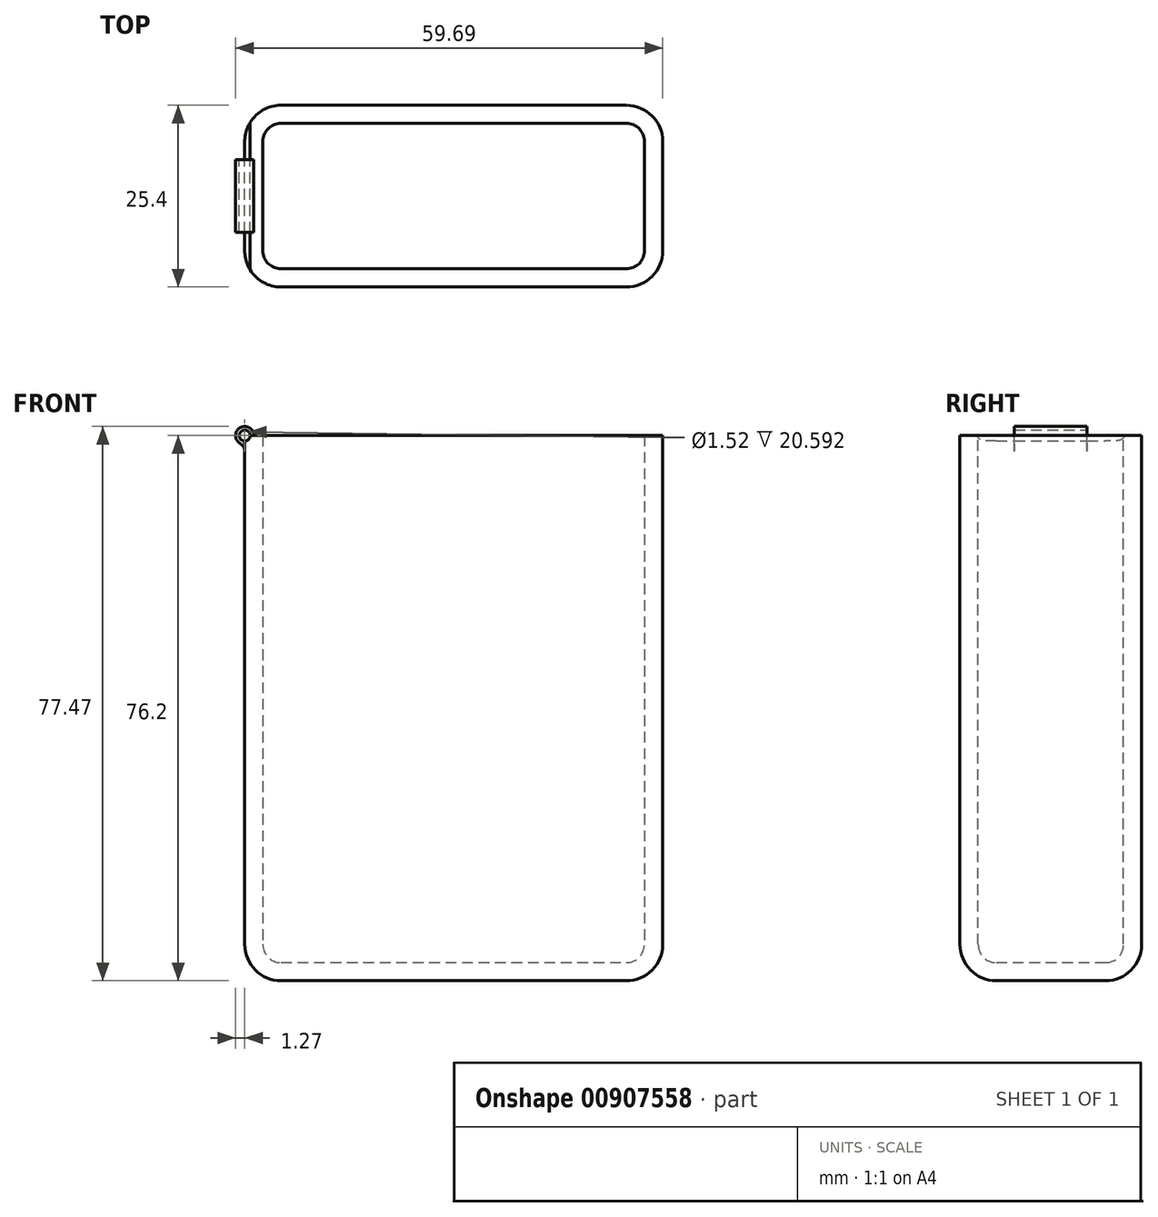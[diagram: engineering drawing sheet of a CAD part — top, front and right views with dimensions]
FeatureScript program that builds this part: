
annotation { "Feature Type Name" : "Feature", "Feature Type Description" : "" }
export const myFeature = defineFeature(function(context is Context, id is Id, definition is map)
    precondition{}
    {
        {
            var Q0;
            Q0=qCreatedBy(makeId("Front.planeOp"),FACE);
            var sketch = newSketch(context, id + "F0", { "sketchPlane" : qUnion([Q0])});
            skLineSegment(sketch, "E0.bottom", {"start": v(-29.21, 38.1) * mm, "end": v(29.21, 38.1) * mm});
            skLineSegment(sketch, "E0.top", {"start": v(-29.2, -38.1) * mm, "end": v(29.21, -38.1) * mm});
            skLineSegment(sketch, "E0.left", {"start": v(-29.21, 38.1) * mm, "end": v(-29.2, -38.1) * mm});
            skLineSegment(sketch, "E0.right", {"start": v(29.2, 38.1) * mm, "end": v(29.21, -38.1) * mm});
            skSolve(sketch);
        }
        {
            var Q0;
            Q0 = qSketchRegion(id + "F0", true);
            extrude(context, id + "F1", {"entities" : qUnion([Q0]), "depth" : 25.4 * mm, "offsetDistance" : 25.4 * mm});
        }
        {
            var Q0;
            Q0=makeQuery(id+"F1.opExtrude","CAP_EDGE",EDGE,{"disambiguationData":[OSD([sQuery(id+"F0.wireOp",EDGE,"E0.left")])],"isStart":false});
            var Q1;
            Q1=makeQuery(id+"F1.opExtrude","CAP_EDGE",EDGE,{"disambiguationData":[OSD([sQuery(id+"F0.wireOp",EDGE,"E0.right")])],"isStart":false});
            var Q2;
            Q2=makeQuery(id+"F1.opExtrude","CAP_EDGE",EDGE,{"disambiguationData":[OSD([sQuery(id+"F0.wireOp",EDGE,"E0.right")])],"isStart":true});
            var Q3;
            Q3=makeQuery(id+"F1.opExtrude","CAP_EDGE",EDGE,{"disambiguationData":[OSD([sQuery(id+"F0.wireOp",EDGE,"E0.left")])],"isStart":true});
            var Q4;
            Q4=makeQuery(id+"F1.opExtrude","SWEPT_FACE",FACE,{"disambiguationData":[OSD([sQuery(id+"F0.wireOp",EDGE,"E0.top")])]});
            fillet(context, id + "F2", {"entities" : qUnion([Q0, Q1, Q2, Q3, Q4]), "radius" : 5.08 * mm, "tangentPropagation" : true, "allowEdgeOverflow" : false});
        }
        {
            var Q0;
            Q0=makeQuery(id+"F1.opExtrude","SWEPT_FACE",FACE,{"disambiguationData":[OSD([sQuery(id+"F0.wireOp",EDGE,"E0.bottom")])]});
            shell(context, id + "F3", {"entities" : qUnion([Q0]), "thickness" : 2.54 * mm});
        }
        {
            var Q0;
            Q0=makeQuery(id+"F1.opExtrude","CAP_FACE",FACE,{"disambiguationData":[OSD([sQuery(id+"F0.wireOp",EDGE,"E0.bottom"),sQuery(id+"F0.wireOp",EDGE,"E0.top"),sQuery(id+"F0.wireOp",EDGE,"E0.left"),sQuery(id+"F0.wireOp",EDGE,"E0.right")])],"isStart":true});
            cPlane(context, id + "F4", {"entities" : qUnion([Q0]), "cplaneType" : CPlaneType.OFFSET, "offset" : 12.7 * mm, "oppositeDirection" : true, "width" : 152.4 * mm, "height" : 152.4 * mm});
        }
        {
            var Q0;
            Q0=qCreatedBy(id+"F4.planeOp",FACE);
            var sketch = newSketch(context, id + "F5", { "sketchPlane" : qUnion([Q0])});
            skCircle(sketch, "E1", {"center": v(29.21, 38.1) * mm, "radius": 1.27 * mm});
            skSolve(sketch);
        }
        {
            var Q0;
            Q0=makeQuery(id+"F5.imprint","IMPRINT",FACE,{"disambiguationData":[TD([[makeQuery(id+"F5.imprint","IMPRINT",EDGE,{"derivedFrom":sQuery(id+"F5.wireOp",EDGE,"E1")}),1.0]])]});
            extrude(context, id + "F6", {"entities" : qUnion([Q0]), "operationType" : NewBodyOperationType.ADD, "endBound" : BoundingType.SYMMETRIC, "depth" : 10.16 * mm, "offsetDistance" : 25.4 * mm});
        }
        {
            var Q0;
            Q0=makeQuery(id+"F6.boolean.opBoolean","INTERSECT",EDGE,{"derivedFrom":[makeQuery(id+"F1.opExtrude","SWEPT_FACE",FACE,{"disambiguationData":[OSD([sQuery(id+"F0.wireOp",EDGE,"E0.left")])]}),makeQuery(id+"F6.opExtrude","SWEPT_FACE",FACE,{"disambiguationData":[OSD([sQuery(id+"F5.wireOp",EDGE,"E1")])]})]});
            fillet(context, id + "F7", {"entities" : qUnion([Q0]), "radius" : 1.27 * mm, "tangentPropagation" : true, "allowEdgeOverflow" : false});
        }
        {
            var Q0;
            Q0=makeQuery(id+"F6.opExtrude","CAP_FACE",FACE,{"disambiguationData":[OSD([sQuery(id+"F5.wireOp",EDGE,"E1")])],"isStart":false});
            var sketch = newSketch(context, id + "F8", { "sketchPlane" : qUnion([Q0])});
            skCircle(sketch, "E2", {"center": v(29.21, 38.1) * mm, "radius": 0.76 * mm});
            skSolve(sketch);
        }
        {
            var Q0;
            Q0 = qSketchRegion(id + "F8", true);
            extrude(context, id + "F9", {"entities" : qUnion([Q0]), "operationType" : NewBodyOperationType.REMOVE, "endBound" : BoundingType.SYMMETRIC, "oppositeDirection" : true, "depth" : 152.4 * mm, "offsetDistance" : 25.4 * mm});
        }
    });
